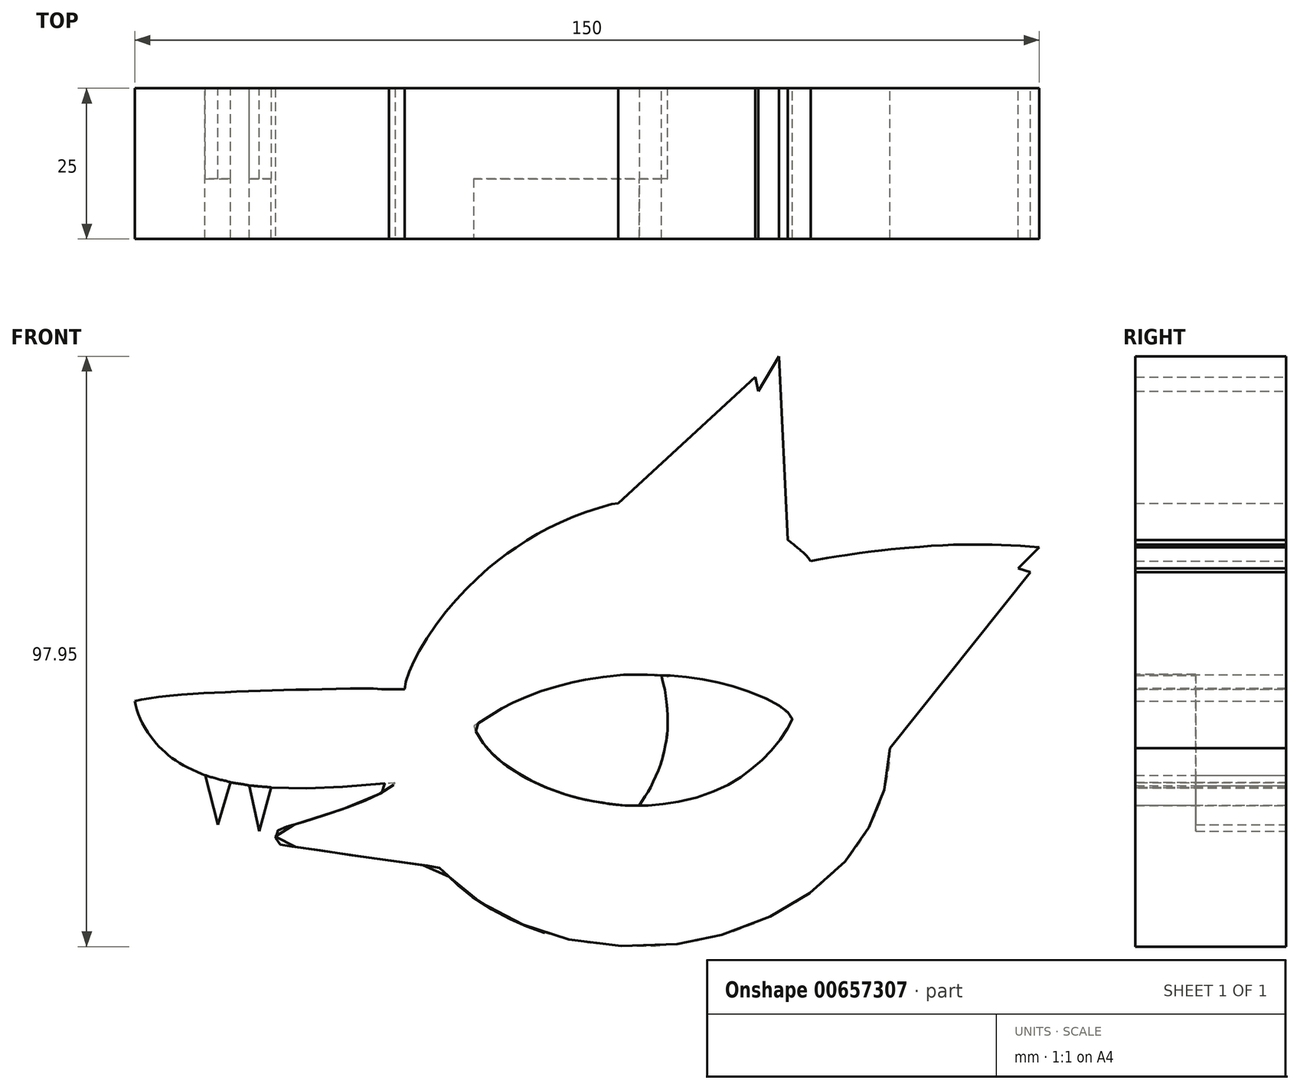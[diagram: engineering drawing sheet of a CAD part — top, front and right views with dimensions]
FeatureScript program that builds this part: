
annotation { "Feature Type Name" : "Feature", "Feature Type Description" : "" }
export const myFeature = defineFeature(function(context is Context, id is Id, definition is map)
    precondition{}
    {
        {
            var Q0;
            Q0=qCreatedBy(makeId("Front.planeOp"),FACE);
            var sketch = newSketch(context, id + "F0", { "sketchPlane" : qUnion([Q0])});
            skFitSpline(sketch, "E0", {"points": [v(-75, -33.85) * mm, v(-72.36, -33.36) * mm, v(-65.99, -32.73) * mm, v(-60.07, -32.4) * mm, v(-53.06, -32.1) * mm, v(-45.48, -31.93) * mm, v(-36.47, -31.77) * mm, v(-32.84, -31.9) * mm], "startDerivative": vector(23.81, 5.16) * mm, "endDerivative": vector(28.04, 0.32) * mm});
            skLineSegment(sketch, "E1", {"start": v(-32.84, -31.9) * mm, "end": v(-30.25, -31.9) * mm});
            skFitSpline(sketch, "E2", {"points": [v(-30.25, -31.9) * mm, v(-30.03, -30.61) * mm, v(-29.12, -28.08) * mm, v(-27.77, -25.44) * mm, v(-24.63, -20.62) * mm, v(-21.2, -16.51) * mm, v(-17.5, -12.83) * mm, v(-14.2, -10.09) * mm, v(-12.5, -8.9) * mm, v(-9.5, -6.91) * mm, v(-6.62, -5.3) * mm, v(-2.8, -3.5) * mm, v(0.99, -2.13) * mm, v(4.6, -1.1) * mm, v(5.19, -1.04) * mm, v(5.16, -1.04) * mm], "startDerivative": vector(3.3, 23.83) * mm, "endDerivative": vector(-5.84, 0.4) * mm});
            skLineSegment(sketch, "E3", {"start": v(5.19, -1.04) * mm, "end": v(27.9, 19.92) * mm});
            skLineSegment(sketch, "E4", {"start": v(27.9, 19.92) * mm, "end": v(28.42, 17.53) * mm});
            skLineSegment(sketch, "E5", {"start": v(28.42, 17.53) * mm, "end": v(31.87, 23.33) * mm});
            skLineSegment(sketch, "E6", {"start": v(31.87, 23.33) * mm, "end": v(33.3, -7.17) * mm});
            skFitSpline(sketch, "E7", {"points": [v(33.3, -7.17) * mm, v(34.17, -7.78) * mm, v(35.04, -8.52) * mm, v(35.9, -9.23) * mm, v(36.6, -9.94) * mm, v(37.14, -10.65) * mm], "startDerivative": vector(4.32, -2.88) * mm, "endDerivative": vector(2.78, -3.86) * mm});
            skFitSpline(sketch, "E8", {"points": [v(37.14, -10.65) * mm, v(41.08, -9.93) * mm, v(48.4, -8.9) * mm, v(53.05, -8.44) * mm, v(59.78, -7.97) * mm, v(65.2, -7.9) * mm, v(70.13, -8) * mm, v(75, -8.36) * mm], "startDerivative": vector(28.5, 5.55) * mm, "endDerivative": vector(35.7, -3.07) * mm});
            skLineSegment(sketch, "E9", {"start": v(75, -8.36) * mm, "end": v(71.56, -11.86) * mm});
            skLineSegment(sketch, "E10", {"start": v(71.56, -11.86) * mm, "end": v(73.56, -12.48) * mm});
            skLineSegment(sketch, "E11", {"start": v(73.56, -12.48) * mm, "end": v(50.29, -41.69) * mm});
            skFitSpline(sketch, "E12", {"points": [v(50.29, -41.69) * mm, v(49.95, -45.76) * mm, v(49.3, -48.6) * mm, v(48.17, -51.87) * mm, v(46.9, -54.6) * mm, v(45.24, -57.24) * mm, v(43.04, -60.23) * mm, v(40.1, -63.1) * mm, v(36.39, -66.18) * mm, v(33.15, -68.16) * mm, v(28.81, -70.39) * mm, v(23.6, -72.32) * mm, v(19.73, -73.33) * mm, v(15.65, -74.13) * mm, v(9.9, -74.62) * mm, v(3.45, -74.34) * mm, v(-1.73, -73.7) * mm, v(-7.33, -72.27) * mm, v(-10.71, -70.94) * mm, v(-14.18, -69.39) * mm, v(-18.84, -66.46) * mm, v(-21.54, -64.32) * mm, v(-23.14, -62.81) * mm, v(-24.35, -61.62) * mm, v(-24.64, -61.5) * mm, v(-27.04, -61.14) * mm, v(-34.83, -60.06) * mm, v(-42.04, -59) * mm, v(-49.95, -57.89) * mm, v(-50.78, -57.75) * mm, v(-51.33, -57.14) * mm, v(-51.64, -56.67) * mm, v(-51.64, -55.9) * mm, v(-51.3, -55.38) * mm, v(-50.97, -55.04) * mm, v(-49.32, -54.57) * mm, v(-45.73, -53.54) * mm, v(-39.95, -51.58) * mm, v(-36.43, -50.24) * mm, v(-33.85, -48.97) * mm, v(-31.9, -47.6) * mm, v(-31.82, -47.48) * mm, v(-31.92, -47.47) * mm, v(-33.26, -47.54) * mm, v(-36.38, -47.78) * mm, v(-40.18, -48.1) * mm, v(-42.72, -48.2) * mm, v(-44.8, -48.28) * mm, v(-48.85, -48.36) * mm, v(-51.36, -48.27) * mm, v(-52.4, -48.2) * mm, v(-52.4, -48.2) * mm], "startDerivative": vector(-10.08, -182.45) * mm, "endDerivative": vector(-1.75, -2.12) * mm});
            skFitSpline(sketch, "E13", {"points": [v(-56.03, -47.89) * mm, v(-56.96, -47.7) * mm, v(-58.2, -47.52) * mm, v(-59.17, -47.35) * mm], "startDerivative": vector(-2.8, 0.61) * mm, "endDerivative": vector(-2.89, 0.56) * mm});
            skFitSpline(sketch, "E14", {"points": [v(-63.37, -46.17) * mm, v(-64.3, -45.8) * mm, v(-66.04, -45) * mm, v(-67.23, -44.4) * mm, v(-68.32, -43.69) * mm, v(-69.33, -42.95) * mm, v(-70.23, -42.14) * mm, v(-71.05, -41.38) * mm, v(-71.84, -40.45) * mm, v(-72.61, -39.45) * mm, v(-73.67, -37.73) * mm, v(-74.27, -36.4) * mm, v(-74.79, -34.95) * mm, v(-75, -33.85) * mm], "startDerivative": vector(-12.75, 4.97) * mm, "endDerivative": vector(-2.23, 15.02) * mm});
            skFitSpline(sketch, "E15", {"points": [v(-63.37, -46.17) * mm, v(-62.75, -46.37) * mm, v(-61.78, -46.66) * mm, v(-60.74, -46.95) * mm, v(-59.8, -47.15) * mm, v(-59.17, -47.35) * mm], "startDerivative": vector(3.35, -1.1) * mm, "endDerivative": vector(3.4, -1.18) * mm});
            skFitSpline(sketch, "E16", {"points": [v(-56.03, -47.89) * mm, v(-55.34, -47.94) * mm, v(-54.37, -48.03) * mm, v(-53.18, -48.12) * mm, v(-52.4, -48.2) * mm], "startDerivative": vector(3.03, -0.2) * mm, "endDerivative": vector(3.12, -0.41) * mm});
            skSolve(sketch);
        }
        {
            var Q0;
            Q0=qCreatedBy(makeId("Front.planeOp"),FACE);
            var sketch = newSketch(context, id + "F1", { "sketchPlane" : qUnion([Q0])});
            skLineSegment(sketch, "E17", {"start": v(-52.4, -48.2) * mm, "end": v(-54.35, -55.45) * mm});
            skLineSegment(sketch, "E18", {"start": v(-54.35, -55.45) * mm, "end": v(-56.03, -47.88) * mm});
            skFitSpline(sketch, "E19", {"points": [v(-56.03, -47.88) * mm, v(-54.62, -47.41) * mm, v(-52.85, -47.46) * mm, v(-52.4, -48.2) * mm], "startDerivative": vector(3.65, 1.52) * mm, "endDerivative": vector(0.96, -3.31) * mm});
            skLineSegment(sketch, "E20", {"start": v(-59.17, -47.35) * mm, "end": v(-61.26, -54.41) * mm});
            skLineSegment(sketch, "E21", {"start": v(-61.26, -54.41) * mm, "end": v(-63.37, -46.17) * mm});
            skFitSpline(sketch, "E22", {"points": [v(-63.37, -46.17) * mm, v(-62.14, -46.04) * mm, v(-60.4, -46.17) * mm, v(-59.17, -47.35) * mm], "startDerivative": vector(3.85, 0.48) * mm, "endDerivative": vector(3.08, -4.1) * mm});
            skSolve(sketch);
        }
        {
            var Q0;
            Q0=qCreatedBy(makeId("Front.planeOp"),FACE);
            var sketch = newSketch(context, id + "F2", { "sketchPlane" : qUnion([Q0])});
            skFitSpline(sketch, "E23", {"points": [v(12.25, -29.51) * mm, v(7.97, -29.46) * mm, v(4.73, -29.63) * mm, v(0.98, -30.1) * mm, v(-0.77, -30.4) * mm, v(-2.22, -30.68) * mm, v(-4.07, -31.15) * mm, v(-6.4, -31.87) * mm, v(-8.34, -32.47) * mm, v(-10.18, -33.23) * mm, v(-11.8, -33.94) * mm, v(-13.1, -34.57) * mm, v(-14.55, -35.32) * mm, v(-18.82, -38.08) * mm, v(-18.83, -38.11) * mm, v(-18.43, -38.89) * mm, v(-17.67, -40.25) * mm, v(-16.77, -41.5) * mm, v(-15.8, -42.5) * mm, v(-14.34, -43.87) * mm, v(-12.83, -44.95) * mm, v(-10.69, -46.33) * mm, v(-8.69, -47.33) * mm, v(-6.28, -48.4) * mm, v(-3.03, -49.53) * mm, v(0, -50.3) * mm, v(2.6, -50.75) * mm, v(5.28, -51.15) * mm, v(8.64, -51.24) * mm, v(8.66, -51.24) * mm, v(9.58, -49.87) * mm, v(10.42, -48.45) * mm, v(11.47, -46.4) * mm, v(12.44, -43.93) * mm, v(13.04, -41.27) * mm, v(13.33, -39.7) * mm, v(13.43, -37.55) * mm, v(13.35, -34.47) * mm, v(12.97, -32.07) * mm, v(12.57, -30.36) * mm, v(12.42, -29.73) * mm, v(12.32, -29.53) * mm, v(12.25, -29.51) * mm]});
            skSolve(sketch);
        }
        {
            var Q0;
            Q0=qCreatedBy(makeId("Front.planeOp"),FACE);
            var sketch = newSketch(context, id + "F3", { "sketchPlane" : qUnion([Q0])});
            skFitSpline(sketch, "E24", {"points": [v(12.24, -29.5) * mm, v(7.97, -29.45) * mm, v(4.72, -29.63) * mm, v(0.98, -30.09) * mm, v(-0.77, -30.4) * mm, v(-2.22, -30.68) * mm, v(-4.07, -31.15) * mm, v(-6.4, -31.86) * mm, v(-8.35, -32.47) * mm, v(-10.19, -33.23) * mm, v(-11.81, -33.94) * mm, v(-13.1, -34.56) * mm, v(-14.55, -35.31) * mm, v(-18.82, -38.08) * mm, v(-18.83, -38.1) * mm, v(-18.44, -38.88) * mm, v(-17.68, -40.24) * mm, v(-16.77, -41.49) * mm, v(-15.81, -42.5) * mm, v(-14.34, -43.87) * mm, v(-12.83, -44.94) * mm, v(-10.69, -46.32) * mm, v(-8.7, -47.33) * mm, v(-6.29, -48.4) * mm, v(-3.04, -49.53) * mm, v(0, -50.3) * mm, v(2.6, -50.74) * mm, v(5.28, -51.14) * mm, v(8.64, -51.23) * mm, v(8.66, -51.23) * mm, v(9.58, -49.86) * mm, v(10.42, -48.44) * mm, v(11.46, -46.4) * mm, v(12.44, -43.93) * mm, v(13.04, -41.26) * mm, v(13.33, -39.69) * mm, v(13.42, -37.54) * mm, v(13.35, -34.46) * mm, v(12.97, -32.06) * mm, v(12.57, -30.36) * mm, v(12.41, -29.72) * mm, v(12.31, -29.53) * mm, v(12.24, -29.5) * mm]});
            skSolve(sketch);
        }
        {
            var Q0;
            Q0=qCreatedBy(makeId("Front.planeOp"),FACE);
            var sketch = newSketch(context, id + "F4", { "sketchPlane" : qUnion([Q0])});
            skFitSpline(sketch, "E25", {"points": [v(8.68, -51.24) * mm, v(9.49, -49.89) * mm, v(10.44, -48.37) * mm, v(11.38, -46.37) * mm, v(12.36, -43.96) * mm, v(12.95, -41.34) * mm, v(13.27, -39.72) * mm, v(13.36, -37.5) * mm, v(13.26, -34.5) * mm, v(12.92, -32.1) * mm, v(12.53, -30.38) * mm, v(12.38, -29.57) * mm, v(12.42, -29.53) * mm, v(13.17, -29.56) * mm, v(14.79, -29.69) * mm, v(17.2, -29.94) * mm, v(19.29, -30.29) * mm, v(21.37, -30.7) * mm, v(23.3, -31.17) * mm, v(25.3, -31.74) * mm, v(27.37, -32.47) * mm, v(30.48, -33.82) * mm, v(31.86, -34.65) * mm, v(32.8, -35.22) * mm, v(33.35, -35.82) * mm, v(33.9, -36.52) * mm, v(34.04, -36.76) * mm, v(34.07, -37) * mm, v(33.67, -37.74) * mm, v(32.7, -39.29) * mm, v(32, -40.31) * mm, v(30.92, -41.68) * mm, v(30.2, -42.52) * mm, v(28.96, -43.8) * mm, v(27.62, -44.9) * mm, v(26.34, -45.88) * mm, v(25.26, -46.66) * mm, v(23.56, -47.66) * mm, v(22, -48.47) * mm, v(19.25, -49.51) * mm, v(16.98, -50.22) * mm, v(13.84, -50.82) * mm, v(12.36, -51.01) * mm, v(10.38, -51.19) * mm, v(9.08, -51.23) * mm, v(8.78, -51.22) * mm, v(8.68, -51.24) * mm]});
            skSolve(sketch);
        }
        {
            var Q0;
            Q0 = qSketchRegion(id + "F0", true);
            extrude(context, id + "F5", {"entities" : qUnion([Q0]), "depth" : 25 * mm, "offsetDistance" : 25 * mm});
        }
        {
            var Q0;
            Q0 = qSketchRegion(id + "F1", true);
            extrude(context, id + "F6", {"entities" : qUnion([Q0]), "operationType" : NewBodyOperationType.ADD, "depth" : 15 * mm, "offsetDistance" : 25 * mm});
        }
        {
            var Q0;
            Q0 = qSketchRegion(id + "F2", true);
            extrude(context, id + "F7", {"entities" : qUnion([Q0]), "operationType" : NewBodyOperationType.REMOVE, "depth" : 25 * mm, "offsetDistance" : 25 * mm});
        }
        {
            var Q0;
            Q0 = qSketchRegion(id + "F3", true);
            extrude(context, id + "F8", {"entities" : qUnion([Q0]), "operationType" : NewBodyOperationType.ADD, "depth" : 15 * mm, "offsetDistance" : 25 * mm});
        }
        {
            var Q0;
            Q0 = qSketchRegion(id + "F4", true);
            extrude(context, id + "F9", {"entities" : qUnion([Q0]), "operationType" : NewBodyOperationType.REMOVE, "oppositeDirection" : true, "depth" : -25 * mm, "offsetDistance" : 25 * mm});
        }
    });
